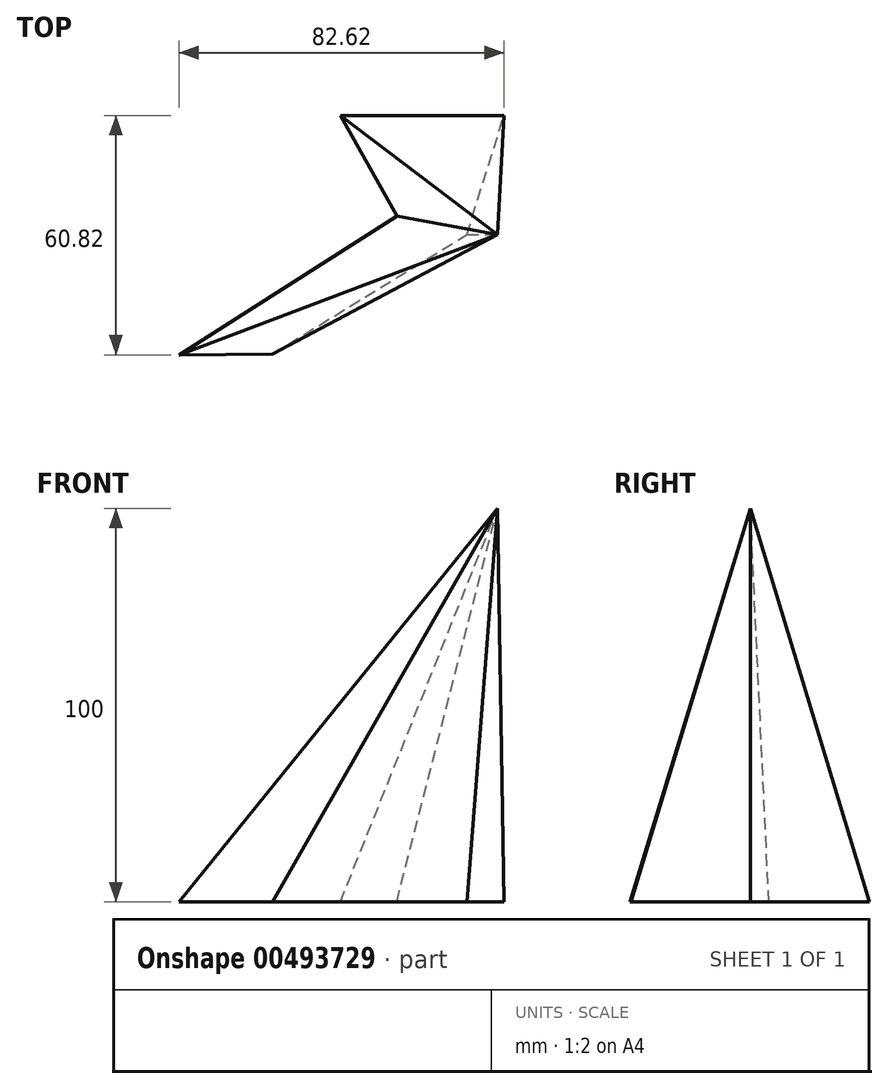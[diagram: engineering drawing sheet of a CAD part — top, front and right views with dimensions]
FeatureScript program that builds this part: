
annotation { "Feature Type Name" : "Feature", "Feature Type Description" : "" }
export const myFeature = defineFeature(function(context is Context, id is Id, definition is map)
    precondition{}
    {
        {
            var Q0;
            Q0=qCreatedBy(makeId("Top.planeOp"),FACE);
            var sketch = newSketch(context, id + "F0", { "sketchPlane" : qUnion([Q0])});
            skLineSegment(sketch, "E0", {"start": v(-70.29, -30.27) * mm, "end": v(-20.94, 0) * mm});
            skLineSegment(sketch, "E1", {"start": v(-20.94, 0) * mm, "end": v(-11.48, 30.27) * mm});
            skLineSegment(sketch, "E2", {"start": v(-11.48, 30.27) * mm, "end": v(-53.07, 30.27) * mm});
            skLineSegment(sketch, "E3", {"start": v(-53.07, 30.27) * mm, "end": v(-38.73, 4.73) * mm});
            skLineSegment(sketch, "E4", {"start": v(-38.73, 4.73) * mm, "end": v(-94.1, -30.55) * mm});
            skLineSegment(sketch, "E5", {"start": v(-94.1, -30.55) * mm, "end": v(-70.29, -30.27) * mm});
            skSolve(sketch);
        }
        {
            var Q0;
            Q0=qCreatedBy(makeId("Top.planeOp"),FACE);
            cPlane(context, id + "F1", {"entities" : qUnion([Q0]), "cplaneType" : CPlaneType.OFFSET, "offset" : 100 * mm, "width" : 150 * mm, "height" : 150 * mm});
        }
        {
            var Q0;
            Q0=qCreatedBy(id+"F1.planeOp",FACE);
            var sketch = newSketch(context, id + "F2", { "sketchPlane" : qUnion([Q0])});
            skPoint(sketch, "E6", {"position": v(-13.1, 0) * mm});
            skSolve(sketch);
        }
        {
            var Q0;
            Q0=makeQuery(id+"F0.imprint","IMPRINT",FACE,{"disambiguationData":[TD([[makeQuery(id+"F0.imprint","IMPRINT",EDGE,{"derivedFrom":sQuery(id+"F0.wireOp",EDGE,"E0")}),1.0]])]});
            var Q1;
            Q1=sQuery(id+"F2.wireOp",VERTEX,"E6");
            loft(context, id + "F3", {"sheetProfilesArray" : [{ "sheetProfileEntities" : qUnion([Q0]) }, { "sheetProfileEntities" : qUnion([Q1]) }]});
        }
    });
